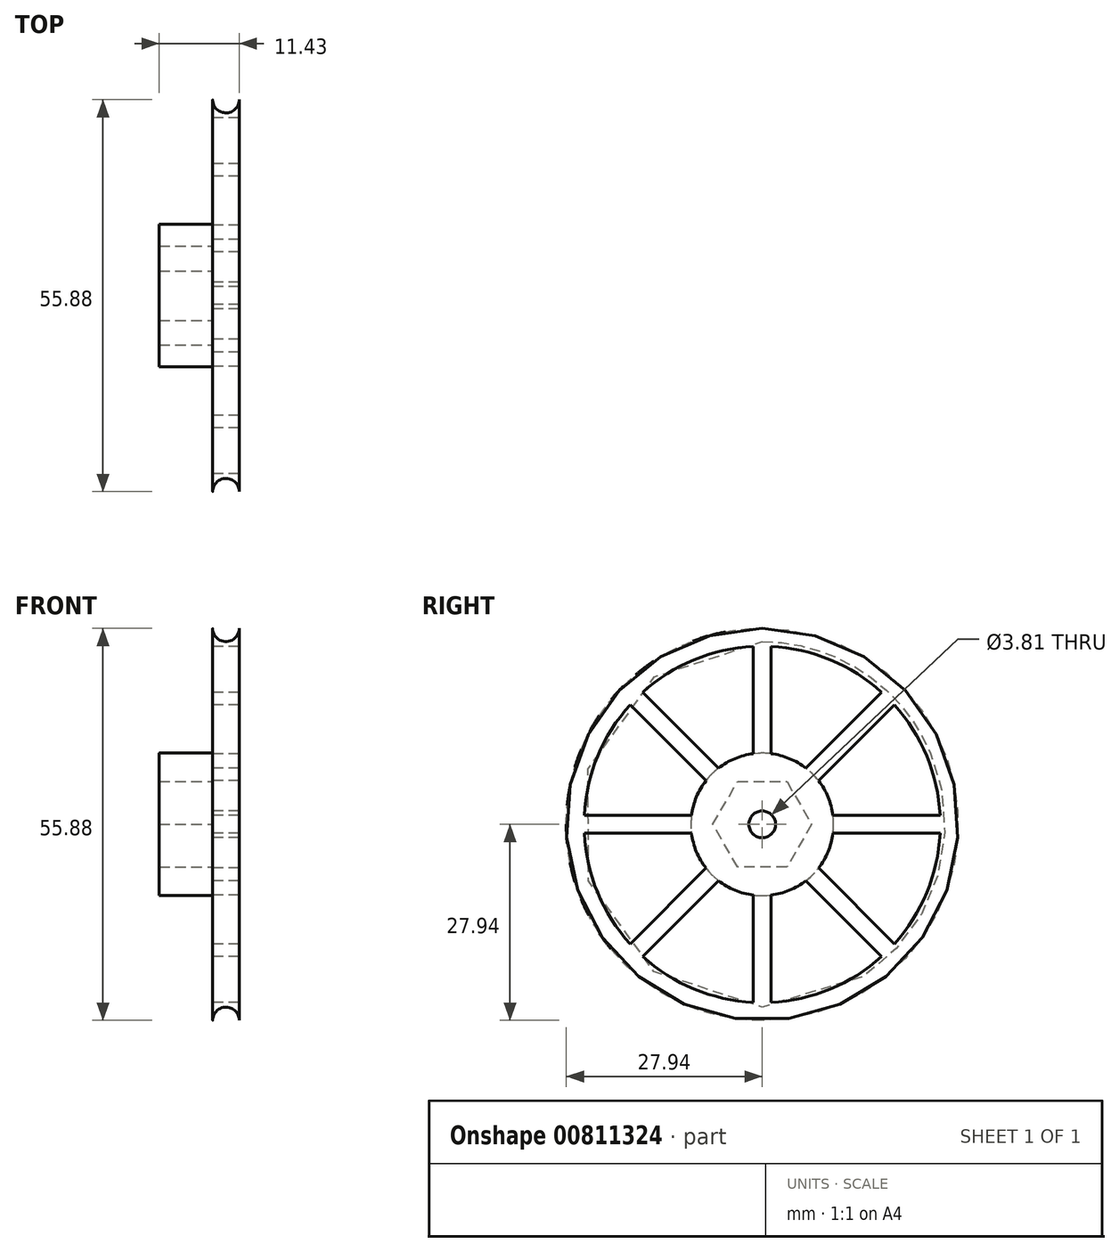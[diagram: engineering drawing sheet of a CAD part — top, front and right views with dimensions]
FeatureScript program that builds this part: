
annotation { "Feature Type Name" : "Feature", "Feature Type Description" : "" }
export const myFeature = defineFeature(function(context is Context, id is Id, definition is map)
    precondition{}
    {
        {
            var Q0;
            Q0=qCreatedBy(makeId("Right.planeOp"),FACE);
            var sketch = newSketch(context, id + "F0", { "sketchPlane" : qUnion([Q0])});
            skCircle(sketch, "E0", {"center": v(0, 0) * mm, "radius": 27.94 * mm});
            skCircle(sketch, "E1", {"center": v(0, 0) * mm, "radius": 1.9 * mm});
            skArc(sketch, "E2", {"start": v(-18.84, 17.04) * mm, "mid": v(-23.47, 9.72) * mm, "end": v(-25.37, 1.27) * mm});
            skLineSegment(sketch, "E3.left", {"start": v(-1.27, 10.08) * mm, "end": v(-1.27, 25.37) * mm});
            skLineSegment(sketch, "E3.right", {"start": v(1.27, 10.08) * mm, "end": v(1.27, 25.37) * mm});
            skLineSegment(sketch, "E4.1.0", {"start": v(8.03, 6.23) * mm, "end": v(18.84, 17.04) * mm});
            skLineSegment(sketch, "E4.1.1", {"start": v(6.23, 8.03) * mm, "end": v(17.04, 18.84) * mm});
            skLineSegment(sketch, "E4.2.0", {"start": v(10.08, -1.27) * mm, "end": v(25.37, -1.27) * mm});
            skLineSegment(sketch, "E4.2.1", {"start": v(10.08, 1.27) * mm, "end": v(25.37, 1.27) * mm});
            skLineSegment(sketch, "E4.anchor1", {"start": v(0, 0) * mm, "end": v(1.27, 3.6) * mm, "construction": true});
            skLineSegment(sketch, "E4.anchor2", {"start": v(0, 0) * mm, "end": v(3.6, -1.27) * mm, "construction": true});
            skLineSegment(sketch, "E5.1.0", {"start": v(8.03, -6.23) * mm, "end": v(18.84, -17.04) * mm});
            skLineSegment(sketch, "E5.1.1", {"start": v(6.23, -8.03) * mm, "end": v(17.04, -18.84) * mm});
            skLineSegment(sketch, "E5.2.0", {"start": v(1.27, -10.08) * mm, "end": v(1.27, -25.37) * mm});
            skLineSegment(sketch, "E5.2.1", {"start": v(-1.27, -10.08) * mm, "end": v(-1.27, -25.37) * mm});
            skLineSegment(sketch, "E5.anchor1", {"start": v(0, 0) * mm, "end": v(3.6, 1.27) * mm, "construction": true});
            skLineSegment(sketch, "E5.anchor2", {"start": v(0, 0) * mm, "end": v(1.27, -3.6) * mm, "construction": true});
            skLineSegment(sketch, "E6.1.0", {"start": v(-6.23, -8.03) * mm, "end": v(-17.04, -18.84) * mm});
            skLineSegment(sketch, "E6.1.1", {"start": v(-8.03, -6.23) * mm, "end": v(-18.84, -17.04) * mm});
            skLineSegment(sketch, "E6.2.0", {"start": v(-10.08, -1.27) * mm, "end": v(-25.37, -1.27) * mm});
            skLineSegment(sketch, "E6.2.1", {"start": v(-10.08, 1.27) * mm, "end": v(-25.37, 1.27) * mm});
            skLineSegment(sketch, "E6.anchor1", {"start": v(0, 0) * mm, "end": v(1.27, -25.37) * mm, "construction": true});
            skLineSegment(sketch, "E6.anchor2", {"start": v(0, 0) * mm, "end": v(-25.37, -1.27) * mm, "construction": true});
            skLineSegment(sketch, "E7.1.0", {"start": v(-8.03, 6.23) * mm, "end": v(-18.84, 17.04) * mm});
            skLineSegment(sketch, "E7.1.1", {"start": v(-6.23, 8.03) * mm, "end": v(-17.04, 18.84) * mm});
            skLineSegment(sketch, "E7.anchor2", {"start": v(0, 0) * mm, "end": v(-18.84, 17.04) * mm, "construction": true});
            skArc(sketch, "E8.trimOffspring", {"start": v(-1.27, 25.37) * mm, "mid": v(-9.72, 23.47) * mm, "end": v(-17.04, 18.84) * mm});
            skArc(sketch, "E9.trimOffspring", {"start": v(17.04, 18.84) * mm, "mid": v(9.72, 23.47) * mm, "end": v(1.27, 25.37) * mm});
            skArc(sketch, "E10.trimOffspring", {"start": v(25.37, 1.27) * mm, "mid": v(23.47, 9.72) * mm, "end": v(18.84, 17.04) * mm});
            skArc(sketch, "E11.trimOffspring", {"start": v(18.84, -17.04) * mm, "mid": v(23.47, -9.72) * mm, "end": v(25.37, -1.27) * mm});
            skArc(sketch, "E12.trimOffspring", {"start": v(1.27, -25.37) * mm, "mid": v(9.72, -23.47) * mm, "end": v(17.04, -18.84) * mm});
            skArc(sketch, "E13.trimOffspring", {"start": v(-17.04, -18.84) * mm, "mid": v(-9.72, -23.47) * mm, "end": v(-1.27, -25.37) * mm});
            skArc(sketch, "E14.trimOffspring", {"start": v(-25.37, -1.27) * mm, "mid": v(-23.47, -9.72) * mm, "end": v(-18.84, -17.04) * mm});
            skArc(sketch, "E15", {"start": v(6.23, 8.03) * mm, "mid": v(3.89, 9.39) * mm, "end": v(1.27, 10.08) * mm});
            skArc(sketch, "E16.trimOffspring", {"start": v(-1.27, 10.08) * mm, "mid": v(-3.89, 9.39) * mm, "end": v(-6.23, 8.03) * mm});
            skArc(sketch, "E17.trimOffspring", {"start": v(-8.03, 6.23) * mm, "mid": v(-9.39, 3.89) * mm, "end": v(-10.08, 1.27) * mm});
            skArc(sketch, "E18.trimOffspring", {"start": v(-10.08, -1.27) * mm, "mid": v(-9.39, -3.89) * mm, "end": v(-8.03, -6.23) * mm});
            skArc(sketch, "E19.trimOffspring", {"start": v(-6.23, -8.03) * mm, "mid": v(-3.89, -9.39) * mm, "end": v(-1.27, -10.08) * mm});
            skArc(sketch, "E20.trimOffspring", {"start": v(1.27, -10.08) * mm, "mid": v(3.89, -9.39) * mm, "end": v(6.23, -8.03) * mm});
            skArc(sketch, "E21.trimOffspring", {"start": v(8.03, -6.23) * mm, "mid": v(9.39, -3.89) * mm, "end": v(10.08, -1.27) * mm});
            skArc(sketch, "E22.trimOffspring", {"start": v(10.08, 1.27) * mm, "mid": v(9.39, 3.89) * mm, "end": v(8.03, 6.23) * mm});
            skPoint(sketch, "E23.orphan", {"position": v(-3.6, 1.27) * mm});
            skSolve(sketch);
        }
        {
            var Q0;
            Q0 = qSketchRegion(id + "F0", true);
            extrude(context, id + "F1", {"entities" : qUnion([Q0]), "depth" : 3.8 * mm, "offsetDistance" : 25.4 * mm});
        }
        {
            var Q0;
            Q0=qCreatedBy(makeId("Front.planeOp"),FACE);
            var sketch = newSketch(context, id + "F2", { "sketchPlane" : qUnion([Q0])});
            skArc(sketch, "E24", {"start": v(3.81, 27.93) * mm, "mid": v(1.9, 26.06) * mm, "end": v(0, 27.93) * mm});
            skLineSegment(sketch, "E25", {"start": v(-7.97, 0) * mm, "end": v(9.15, 0) * mm, "construction": true});
            skLineSegment(sketch, "E26", {"start": v(3.81, 27.93) * mm, "end": v(0, 27.93) * mm});
            skSolve(sketch);
        }
        {
            var Q0;
            Q0 = qSketchRegion(id + "F2", true);
            var Q1;
            Q1=sQuery(id+"F2.wireOp",EDGE,"E25");
            revolve(context, id + "F3", {"operationType" : NewBodyOperationType.REMOVE, "surfaceOperationType" : NewSurfaceOperationType.NEW, "entities" : qUnion([Q0]), "axis" : qUnion([Q1]), "revolveType" : RevolveType.FULL});
        }
        {
            var Q0;
            Q0=qCreatedBy(makeId("Right.planeOp"),FACE);
            var sketch = newSketch(context, id + "F4", { "sketchPlane" : qUnion([Q0])});
            skCircle(sketch, "E27", {"center": v(0, 0) * mm, "radius": 6.1 * mm, "construction": true});
            skLineSegment(sketch, "E28.0", {"start": v(-3.52, 6.1) * mm, "end": v(3.52, 6.1) * mm});
            skLineSegment(sketch, "E28.1", {"start": v(3.52, 6.1) * mm, "end": v(7.04, 0) * mm});
            skLineSegment(sketch, "E28.2", {"start": v(7.04, 0) * mm, "end": v(3.52, -6.1) * mm});
            skLineSegment(sketch, "E28.3", {"start": v(3.52, -6.1) * mm, "end": v(-3.52, -6.1) * mm});
            skLineSegment(sketch, "E28.4", {"start": v(-3.52, -6.1) * mm, "end": v(-7.04, 0) * mm});
            skLineSegment(sketch, "E28.5", {"start": v(-7.04, 0) * mm, "end": v(-3.52, 6.1) * mm});
            skPoint(sketch, "E28.0.midPoint", {"position": v(0, 6.1) * mm});
            skCircle(sketch, "E29", {"center": v(0, 0) * mm, "radius": 10.16 * mm});
            skSolve(sketch);
        }
        {
            var Q0;
            Q0 = qSketchRegion(id + "F4", true);
            extrude(context, id + "F5", {"entities" : qUnion([Q0]), "operationType" : NewBodyOperationType.ADD, "oppositeDirection" : true, "depth" : 7.62 * mm, "offsetDistance" : 25.4 * mm});
        }
    });
